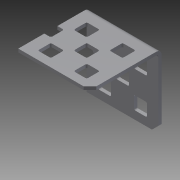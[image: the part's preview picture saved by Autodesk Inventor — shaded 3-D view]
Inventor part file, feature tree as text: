
AUTODESK INVENTOR PART (.ipt)
format: ipt  version: 2014 SP1 (Build 180222100, 222)  size: 795,136 bytes
history: native  units: in
note: dims shown in document units (in); Inventor stores cm internally (conversion verified against a paired STEP export)
features: other x1, imported_body x1, extrude x1, sketch x1
ambient origin geometry x8: Origin, YZ Plane, XZ Plane, XY Plane, X Axis, Y Axis, Z Axis, Center Point
bodies: Body1 (feature_tree)
feature tree (4):
  parser-record x1  (decoder bookkeeping rows leaked as tree rows — omitted from the tree; the rows remain in map.json)
  imported_body  "Base1"
  extrude  "Extrusion1"  Depth=1.0in
  sketch  "Sketch1"  dims[d0=1.0in d1=0.0in d2=6.5in]
